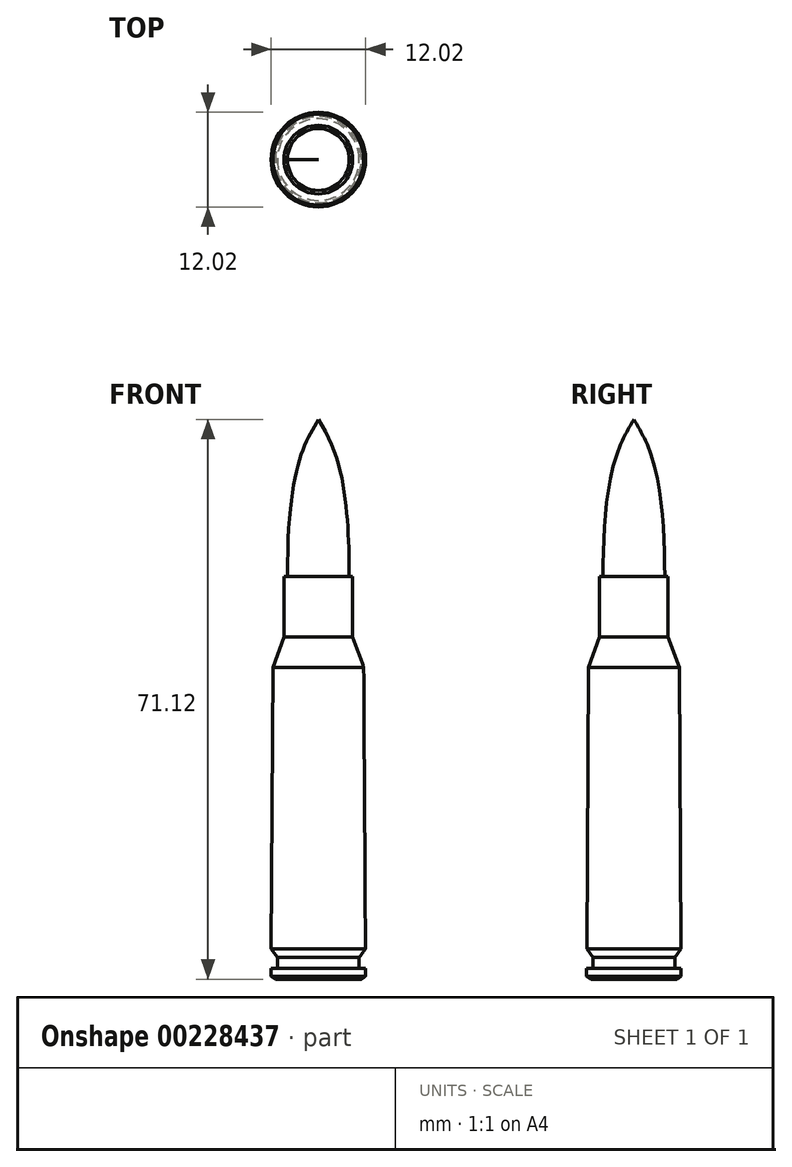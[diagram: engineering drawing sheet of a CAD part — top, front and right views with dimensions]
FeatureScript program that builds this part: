
annotation { "Feature Type Name" : "Feature", "Feature Type Description" : "" }
export const myFeature = defineFeature(function(context is Context, id is Id, definition is map)
    precondition{}
    {
        {
            var Q0;
            Q0=qCreatedBy(makeId("Top.planeOp"),FACE);
            cPlane(context, id + "F0", {"entities" : qUnion([Q0]), "cplaneType" : CPlaneType.OFFSET, "offset" : 51.18 * mm, "oppositeDirection" : true, "width" : 152.4 * mm, "height" : 152.4 * mm});
        }
        {
            var Q0;
            Q0=qCreatedBy(makeId("Top.planeOp"),FACE);
            var sketch = newSketch(context, id + "F1", { "sketchPlane" : qUnion([Q0])});
            skCircle(sketch, "E0", {"center": v(0, 0) * mm, "radius": 3.92 * mm});
            skSolve(sketch);
        }
        {
            var Q0;
            Q0=qCreatedBy(id+"F0.planeOp",FACE);
            cPlane(context, id + "F2", {"entities" : qUnion([Q0]), "cplaneType" : CPlaneType.OFFSET, "offset" : 71.12 * mm, "width" : 150 * mm, "height" : 150 * mm});
        }
        {
            var Q0;
            Q0=qCreatedBy(id+"F2.planeOp",FACE);
            var sketch = newSketch(context, id + "F3", { "sketchPlane" : qUnion([Q0])});
            skPoint(sketch, "E1", {"position": v(0, 0) * mm});
            skSolve(sketch);
        }
        {
            var Q0;
            Q0=makeQuery(id+"F1.imprint","IMPRINT",FACE,{"disambiguationData":[TD([[makeQuery(id+"F1.imprint","IMPRINT",EDGE,{"derivedFrom":sQuery(id+"F1.wireOp",EDGE,"E0")}),1.0]])]});
            var Q1;
            Q1=sQuery(id+"F3.wireOp",VERTEX,"E1");
            loft(context, id + "F4", {"startCondition" : LoftEndDerivativeType.NORMAL_TO_PROFILE, "startMagnitude" : 2, "sheetProfilesArray" : [{ "sheetProfileEntities" : qUnion([Q0]) }, { "sheetProfileEntities" : qUnion([Q1]) }]});
        }
        {
            var Q0;
            Q0=qCreatedBy(makeId("Top.planeOp"),FACE);
            var sketch = newSketch(context, id + "F5", { "sketchPlane" : qUnion([Q0])});
            skCircle(sketch, "E2", {"center": v(0, 0) * mm, "radius": 4.36 * mm});
            skSolve(sketch);
        }
        {
            var Q0;
            Q0=qCreatedBy(id+"F0.planeOp",FACE);
            cPlane(context, id + "F6", {"entities" : qUnion([Q0]), "cplaneType" : CPlaneType.OFFSET, "offset" : 43.48 * mm, "width" : 150 * mm, "height" : 150 * mm});
        }
        {
            var Q0;
            Q0=qCreatedBy(id+"F6.planeOp",FACE);
            var sketch = newSketch(context, id + "F7", { "sketchPlane" : qUnion([Q0])});
            skCircle(sketch, "E3", {"center": v(0, 0) * mm, "radius": 4.36 * mm});
            skSolve(sketch);
        }
        {
            var Q1;
            Q1=makeQuery(id+"F5.imprint","IMPRINT",FACE,{"disambiguationData":[TD([[makeQuery(id+"F5.imprint","IMPRINT",EDGE,{"derivedFrom":sQuery(id+"F5.wireOp",EDGE,"E2")}),1.0]])]});
            var Q2;
            Q2=makeQuery(id+"F7.imprint","IMPRINT",FACE,{"disambiguationData":[TD([[makeQuery(id+"F7.imprint","IMPRINT",EDGE,{"derivedFrom":sQuery(id+"F7.wireOp",EDGE,"E3")}),1.0]])]});
            loft(context, id + "F8", {"operationType" : NewBodyOperationType.ADD, "sheetProfilesArray" : [{ "sheetProfileEntities" : qUnion([Q1]) }, { "sheetProfileEntities" : qUnion([Q2]) }]});
        }
        {
            var Q0;
            Q0=qCreatedBy(id+"F0.planeOp",FACE);
            cPlane(context, id + "F9", {"entities" : qUnion([Q0]), "cplaneType" : CPlaneType.OFFSET, "offset" : 39.62 * mm, "width" : 150 * mm, "height" : 150 * mm});
        }
        {
            var Q0;
            Q0=qCreatedBy(id+"F9.planeOp",FACE);
            var sketch = newSketch(context, id + "F10", { "sketchPlane" : qUnion([Q0])});
            skCircle(sketch, "E4", {"center": v(0, 0) * mm, "radius": 5.76 * mm});
            skSolve(sketch);
        }
        {
            var Q1;
            Q1=makeQuery(id+"F8.opLoft","CAP_FACE",FACE,{"disambiguationData":[OSD([makeQuery(id+"F7.imprint","IMPRINT",FACE,{"disambiguationData":[TD([[makeQuery(id+"F7.imprint","IMPRINT",EDGE,{"derivedFrom":sQuery(id+"F7.wireOp",EDGE,"E3")}),1.0]])]})])],"isStart":true});
            var Q2;
            Q2=makeQuery(id+"F10.imprint","IMPRINT",FACE,{"disambiguationData":[TD([[makeQuery(id+"F10.imprint","IMPRINT",EDGE,{"derivedFrom":sQuery(id+"F10.wireOp",EDGE,"E4")}),1.0]])]});
            loft(context, id + "F11", {"operationType" : NewBodyOperationType.ADD, "sheetProfilesArray" : [{ "sheetProfileEntities" : qUnion([Q1]) }, { "sheetProfileEntities" : qUnion([Q2]) }]});
        }
        {
            var Q0;
            Q0=qCreatedBy(id+"F0.planeOp",FACE);
            cPlane(context, id + "F12", {"entities" : qUnion([Q0]), "cplaneType" : CPlaneType.OFFSET, "offset" : 3.85 * mm, "width" : 150 * mm, "height" : 150 * mm});
        }
        {
            var Q0;
            Q0=qCreatedBy(id+"F12.planeOp",FACE);
            var sketch = newSketch(context, id + "F13", { "sketchPlane" : qUnion([Q0])});
            skCircle(sketch, "E5", {"center": v(0, 0) * mm, "radius": 5.98 * mm});
            skSolve(sketch);
        }
        {
            var Q1;
            Q1=makeQuery(id+"F11.opLoft","CAP_FACE",FACE,{"disambiguationData":[OSD([makeQuery(id+"F10.imprint","IMPRINT",FACE,{"disambiguationData":[TD([[makeQuery(id+"F10.imprint","IMPRINT",EDGE,{"derivedFrom":sQuery(id+"F10.wireOp",EDGE,"E4")}),1.0]])]})])],"isStart":true});
            var Q2;
            Q2=makeQuery(id+"F13.imprint","IMPRINT",FACE,{"disambiguationData":[TD([[makeQuery(id+"F13.imprint","IMPRINT",EDGE,{"derivedFrom":sQuery(id+"F13.wireOp",EDGE,"E5")}),1.0]])]});
            loft(context, id + "F14", {"operationType" : NewBodyOperationType.ADD, "sheetProfilesArray" : [{ "sheetProfileEntities" : qUnion([Q1]) }, { "sheetProfileEntities" : qUnion([Q2]) }]});
        }
        {
            var Q0;
            Q0=qCreatedBy(id+"F0.planeOp",FACE);
            cPlane(context, id + "F15", {"entities" : qUnion([Q0]), "cplaneType" : CPlaneType.OFFSET, "offset" : 2.77 * mm, "width" : 150 * mm, "height" : 150 * mm});
        }
        {
            var Q0;
            Q0=qCreatedBy(id+"F15.planeOp",FACE);
            var sketch = newSketch(context, id + "F16", { "sketchPlane" : qUnion([Q0])});
            skCircle(sketch, "E6", {"center": v(0, 0) * mm, "radius": 5.2 * mm});
            skSolve(sketch);
        }
        {
            var Q1;
            Q1=makeQuery(id+"F14.opLoft","CAP_FACE",FACE,{"disambiguationData":[OSD([makeQuery(id+"F13.imprint","IMPRINT",FACE,{"disambiguationData":[TD([[makeQuery(id+"F13.imprint","IMPRINT",EDGE,{"derivedFrom":sQuery(id+"F13.wireOp",EDGE,"E5")}),1.0]])]})])],"isStart":true});
            var Q2;
            Q2=makeQuery(id+"F16.imprint","IMPRINT",FACE,{"disambiguationData":[TD([[makeQuery(id+"F16.imprint","IMPRINT",EDGE,{"derivedFrom":sQuery(id+"F16.wireOp",EDGE,"E6")}),1.0]])]});
            loft(context, id + "F17", {"operationType" : NewBodyOperationType.ADD, "sheetProfilesArray" : [{ "sheetProfileEntities" : qUnion([Q1]) }, { "sheetProfileEntities" : qUnion([Q2]) }]});
        }
        {
            var Q0;
            Q0=makeQuery(id+"F17.opLoft","CAP_FACE",FACE,{"disambiguationData":[OSD([makeQuery(id+"F16.imprint","IMPRINT",FACE,{"disambiguationData":[TD([[makeQuery(id+"F16.imprint","IMPRINT",EDGE,{"derivedFrom":sQuery(id+"F16.wireOp",EDGE,"E6")}),1.0]])]})])],"isStart":true});
            extrude(context, id + "F18", {"entities" : qUnion([Q0]), "operationType" : NewBodyOperationType.ADD, "depth" : 1.4 * mm});
        }
        {
            var Q0;
            Q0=makeQuery(id+"F18.opExtrude","CAP_FACE",FACE,{"disambiguationData":[OSD([makeQuery(id+"F16.imprint","IMPRINT",FACE,{"disambiguationData":[TD([[makeQuery(id+"F16.imprint","IMPRINT",EDGE,{"derivedFrom":sQuery(id+"F16.wireOp",EDGE,"E6")}),1.0]])]})])],"isStart":false});
            var sketch = newSketch(context, id + "F19", { "sketchPlane" : qUnion([Q0])});
            skCircle(sketch, "E7", {"center": v(0, 0) * mm, "radius": 6 * mm});
            skSolve(sketch);
        }
        {
            var Q0;
            Q0=makeQuery(id+"F19.imprint","IMPRINT",FACE,{"disambiguationData":[TD([[makeQuery(id+"F19.imprint","IMPRINT",EDGE,{"derivedFrom":sQuery(id+"F19.wireOp",EDGE,"E7")}),1.0]])]});
            var Q1;
            Q1=makeQuery(id+"F19.imprint","IMPRINT",FACE,{"disambiguationData":[TD([[makeQuery(id+"F19.imprint","IMPRINT",EDGE,{"derivedFrom":makeQuery(id+"F18.opExtrude","CAP_EDGE",EDGE,{"disambiguationData":[OSD([sQuery(id+"F5.wireOp",EDGE,"E2"),sQuery(id+"F7.wireOp",EDGE,"E3"),sQuery(id+"F10.wireOp",EDGE,"E4"),sQuery(id+"F13.wireOp",EDGE,"E5"),sQuery(id+"F16.wireOp",EDGE,"E6")])],"isStart":false})}),1.0]])]});
            extrude(context, id + "F20", {"entities" : qUnion([Q0, Q1]), "operationType" : NewBodyOperationType.ADD, "depth" : 0.99 * mm});
        }
        {
            var Q0;
            Q0=qCreatedBy(id+"F0.planeOp",FACE);
            var sketch = newSketch(context, id + "F21", { "sketchPlane" : qUnion([Q0])});
            skCircle(sketch, "E8", {"center": v(0, 0) * mm, "radius": 5.46 * mm});
            skSolve(sketch);
        }
        {
            var Q1;
            Q1=makeQuery(id+"F20.opExtrude","CAP_FACE",FACE,{"disambiguationData":[OSD([sQuery(id+"F19.wireOp",EDGE,"E7")])],"isStart":false});
            var Q2;
            Q2=makeQuery(id+"F21.imprint","IMPRINT",FACE,{"disambiguationData":[TD([[makeQuery(id+"F21.imprint","IMPRINT",EDGE,{"derivedFrom":sQuery(id+"F21.wireOp",EDGE,"E8")}),1.0]])]});
            loft(context, id + "F22", {"operationType" : NewBodyOperationType.ADD, "sheetProfilesArray" : [{ "sheetProfileEntities" : qUnion([Q1]) }, { "sheetProfileEntities" : qUnion([Q2]) }]});
        }
    });
